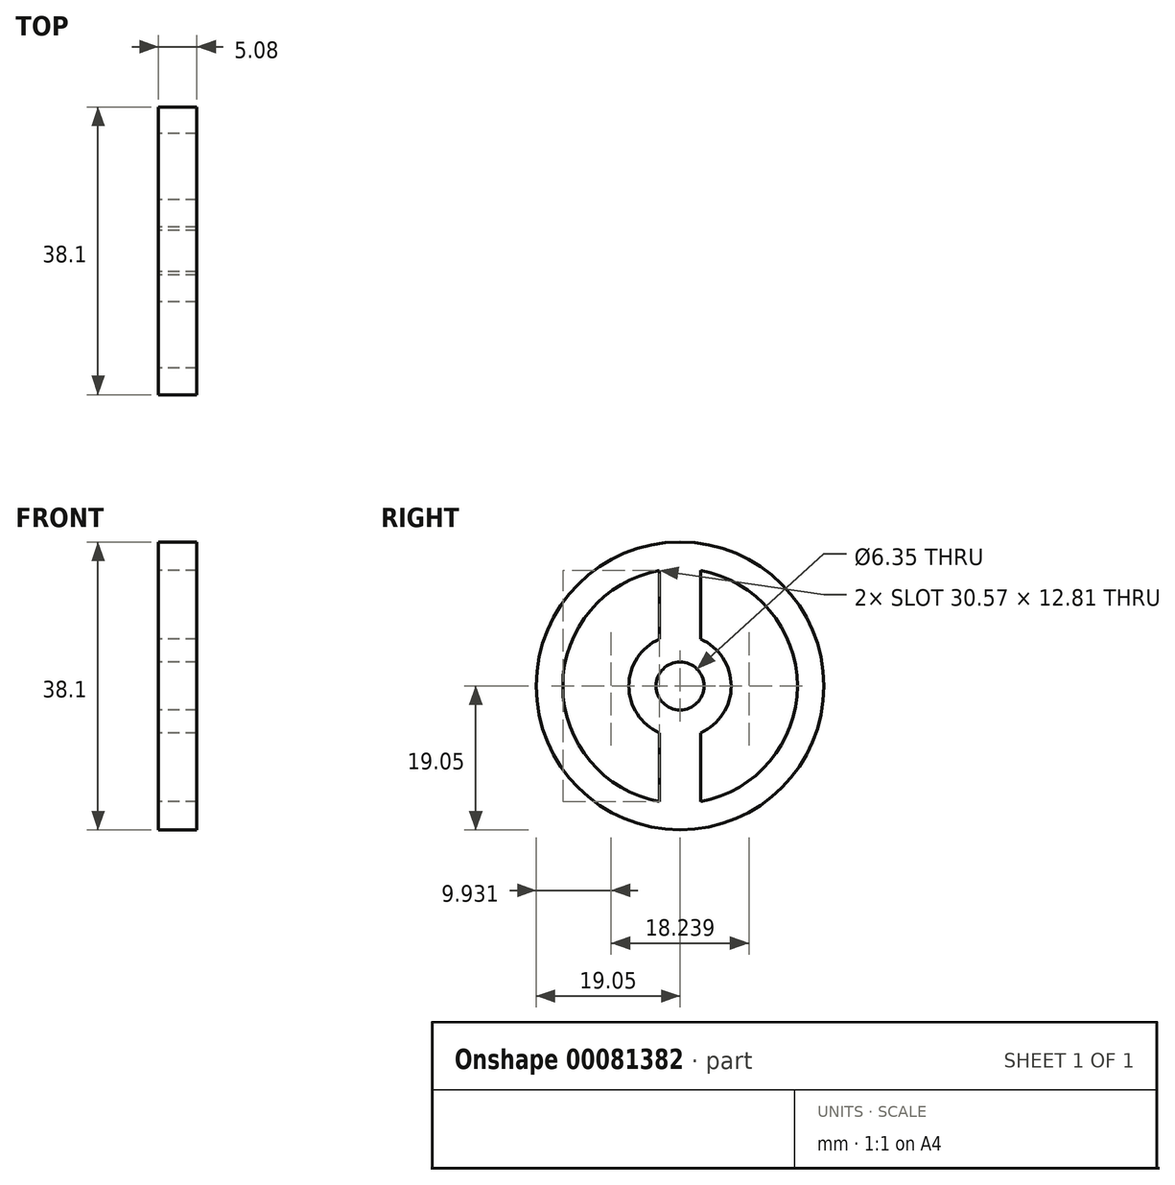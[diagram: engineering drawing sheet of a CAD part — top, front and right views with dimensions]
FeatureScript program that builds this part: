
annotation { "Feature Type Name" : "Feature", "Feature Type Description" : "" }
export const myFeature = defineFeature(function(context is Context, id is Id, definition is map)
    precondition{}
    {
        {
            var Q0;
            Q0=qCreatedBy(makeId("Right.planeOp"),FACE);
            var sketch = newSketch(context, id + "F0", { "sketchPlane" : qUnion([Q0])});
            skCircle(sketch, "E0", {"center": v(0, 0) * mm, "radius": 19.05 * mm});
            skArc(sketch, "E1", {"start": v(-2.71, 15.29) * mm, "mid": v(-15.53, 0) * mm, "end": v(-2.71, -15.29) * mm});
            skArc(sketch, "E2", {"start": v(-2.71, 6.2) * mm, "mid": v(-6.77, 0) * mm, "end": v(-2.71, -6.2) * mm});
            skCircle(sketch, "E3", {"center": v(0, 0) * mm, "radius": 3.18 * mm});
            skLineSegment(sketch, "E4", {"start": v(-2.71, 6.2) * mm, "end": v(-2.71, 15.29) * mm});
            skLineSegment(sketch, "E5", {"start": v(-2.71, -6.2) * mm, "end": v(-2.71, -15.29) * mm});
            skLineSegment(sketch, "E6", {"start": v(2.71, 15.29) * mm, "end": v(2.71, 6.2) * mm});
            skLineSegment(sketch, "E7", {"start": v(2.72, -6.2) * mm, "end": v(2.72, -15.29) * mm});
            skArc(sketch, "E8.trimOffspring", {"start": v(2.72, -6.2) * mm, "mid": v(6.77, 0) * mm, "end": v(2.71, 6.2) * mm});
            skArc(sketch, "E9.trimOffspring", {"start": v(2.72, -15.29) * mm, "mid": v(15.53, 0) * mm, "end": v(2.71, 15.29) * mm});
            skSolve(sketch);
        }
        {
            var Q0;
            Q0 = qSketchRegion(id + "F0", true);
            extrude(context, id + "F1", {"entities" : qUnion([Q0]), "depth" : 5.08 * mm});
        }
    });
